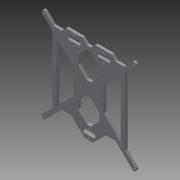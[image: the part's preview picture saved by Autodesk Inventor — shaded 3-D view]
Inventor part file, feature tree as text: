
AUTODESK INVENTOR PART (.ipt)
format: ipt  version: 2015 (Build 190159000, 159)  size: 271,872 bytes
history: native  units: mm
features: chamfer x4, sketch x4, extrude x3, hole x1
ambient origin geometry x8: Origin, YZ Plane, XZ Plane, XY Plane, X Axis, Y Axis, Z Axis, Center Point
bodies: Solid1 (feature_tree)
feature tree (12):
  extrude  "Extrusion1"  Depth=220.0mm
  extrude  "Extrusion2"  Depth=6.0mm
  chamfer  "Chamfer3"  Distance=7.0mm
  chamfer  "Chamfer4"  Distance=10.0mm
  chamfer  "Chamfer5"  Distance=40.0mm
  chamfer  "Chamfer6"  Angle=135.0deg  [1 undecoded]
  extrude  "Extrusion3"  Depth=15.0mm
  hole  "Hole1"  [1 undecoded]
  sketch  "Sketch1"  dims[d0=220.0mm d1=220.0mm]
  sketch  "Sketch2"  dims[d2=6.0mm d3=0.0mm d4=206.0mm]
  sketch  "Sketch3"  dims[d6=25.0mm]
  sketch  "Sketch4"  dims[d7=135.0deg d8=7.0mm d10=10.0mm d11=40.0mm d12=135.0deg d13=7.0mm d14=20.0mm d15=135.0deg d16=38.0mm d17=10.0mm d20=25.0mm d21=60.0mm d22=10.0mm d23=135.0deg d24=57.0mm d25=7.0mm d26=40.0mm d27=10.0mm d28=30.0mm d29=0.0mm d30=0.0mm d37=3.0mm d38=4.0mm d39=45.0deg d40=3.0mm d41=4.0mm d42=45.0deg d43=3.0mm d44=4.0mm d45=45.0deg d46=3.0mm d47=4.0mm d48=45.0deg d50=10.0mm d51=31.0mm d52=10.0mm d56=4.0mm d57=4.0mm d58=10.0mm d60=14.0mm d61=6.0mm d62=0.0mm d63=5.0mm d64=5.0mm d65=5.0mm d66=5.0mm d67=5.0mm d68=11.5mm d70=20.037mm d71=5.642mm d72=5.642mm d73=5.0mm d74=3.6mm d75=6.0mm d76=4.0mm d77=2.0mm d78=90.0deg d79=8.0mm d80=20.594885mm d81=15.0mm]
note: 2 required parameter values undecoded (feature->parameter linkage not recoverable at this tier; creation-order binding heuristic only, values carry confidence <= 0.55)
